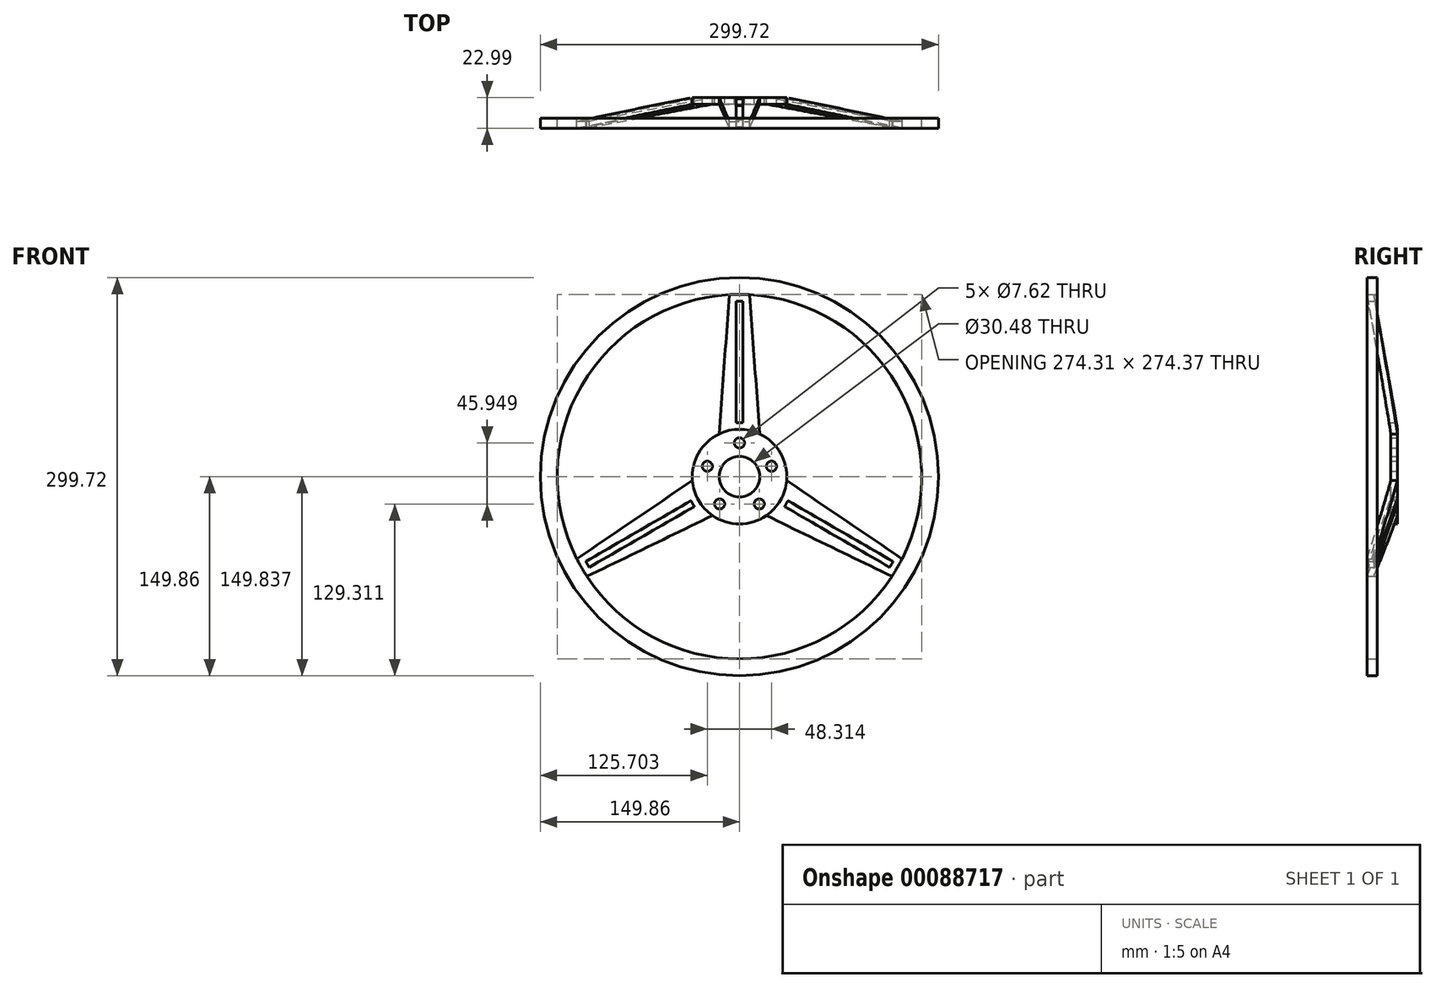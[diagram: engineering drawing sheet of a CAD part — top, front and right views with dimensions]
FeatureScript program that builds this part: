
annotation { "Feature Type Name" : "Feature", "Feature Type Description" : "" }
export const myFeature = defineFeature(function(context is Context, id is Id, definition is map)
    precondition{}
    {
        {
            var Q0;
            Q0=qCreatedBy(makeId("Top.planeOp"),FACE);
            var sketch = newSketch(context, id + "F0", { "sketchPlane" : qUnion([Q0])});
            skLineSegment(sketch, "E0", {"start": v(0, 33.06) * mm, "end": v(0, -40.5) * mm});
            skLineSegment(sketch, "E1.bottom", {"start": v(-15.24, 0) * mm, "end": v(-35.56, 0) * mm});
            skLineSegment(sketch, "E1.top", {"start": v(-15.24, -5.08) * mm, "end": v(-35.6, -5.08) * mm});
            skLineSegment(sketch, "E1.left", {"start": v(-15.24, 0) * mm, "end": v(-15.24, -5.08) * mm});
            skLineSegment(sketch, "E2", {"start": v(-35.56, 0) * mm, "end": v(-137.16, -17.91) * mm});
            skLineSegment(sketch, "E3", {"start": v(-35.6, -5.08) * mm, "end": v(-137.16, -22.99) * mm});
            skLineSegment(sketch, "E4.bottom", {"start": v(-137.16, -22.99) * mm, "end": v(-149.86, -22.99) * mm});
            skLineSegment(sketch, "E4.top", {"start": v(-137.16, -15.37) * mm, "end": v(-149.86, -15.37) * mm});
            skLineSegment(sketch, "E4.left", {"start": v(-137.16, -17.91) * mm, "end": v(-137.16, -15.37) * mm});
            skLineSegment(sketch, "E4.right", {"start": v(-149.86, -22.99) * mm, "end": v(-149.86, -15.37) * mm});
            skSolve(sketch);
        }
        {
            var Q0;
            Q0=makeQuery(id+"F0.imprint","IMPRINT",FACE,{"disambiguationData":[TD([[makeQuery(id+"F0.imprint","IMPRINT",EDGE,{"derivedFrom":sQuery(id+"F0.wireOp",EDGE,"E1.bottom")}),1.0]])]});
            var Q1;
            Q1=sQuery(id+"F0.wireOp",EDGE,"E0");
            revolve(context, id + "F1", {"entities" : qUnion([Q0]), "axis" : qUnion([Q1]), "revolveType" : RevolveType.FULL});
        }
        {
            var Q0;
            Q0=makeQuery(id+"F1.opRevolve","SWEPT_FACE",FACE,{"disambiguationData":[OSD([sQuery(id+"F0.wireOp",EDGE,"E1.top")])]});
            var sketch = newSketch(context, id + "F2", { "sketchPlane" : qUnion([Q0])});
            skLineSegment(sketch, "E5", {"start": v(0, 35.6) * mm, "end": v(0, 137.2) * mm});
            skLineSegment(sketch, "E6", {"start": v(0, 137.2) * mm, "end": v(-7.62, 137.2) * mm});
            skLineSegment(sketch, "E7", {"start": v(0, 137.2) * mm, "end": v(7.62, 137.2) * mm});
            skLineSegment(sketch, "E8", {"start": v(-7.62, 137.2) * mm, "end": v(-15.24, 32.18) * mm});
            skLineSegment(sketch, "E9", {"start": v(7.62, 137.2) * mm, "end": v(15.24, 32.18) * mm});
            skLineSegment(sketch, "E10.1.0", {"start": v(-115.01, -75.2) * mm, "end": v(-20.25, -29.29) * mm});
            skLineSegment(sketch, "E10.1.1", {"start": v(-30.84, -17.8) * mm, "end": v(-118.82, -68.6) * mm});
            skLineSegment(sketch, "E10.1.2", {"start": v(-122.63, -62) * mm, "end": v(-35.49, -2.9) * mm});
            skLineSegment(sketch, "E10.1.3", {"start": v(-118.82, -68.6) * mm, "end": v(-122.63, -62) * mm});
            skLineSegment(sketch, "E10.1.4", {"start": v(-118.82, -68.6) * mm, "end": v(-115.01, -75.2) * mm});
            skLineSegment(sketch, "E10.2.0", {"start": v(122.63, -62) * mm, "end": v(35.49, -2.9) * mm});
            skLineSegment(sketch, "E10.2.1", {"start": v(30.84, -17.8) * mm, "end": v(118.82, -68.6) * mm});
            skLineSegment(sketch, "E10.2.2", {"start": v(115.01, -75.2) * mm, "end": v(20.25, -29.29) * mm});
            skLineSegment(sketch, "E10.2.3", {"start": v(118.82, -68.6) * mm, "end": v(115.01, -75.2) * mm});
            skLineSegment(sketch, "E10.2.4", {"start": v(118.82, -68.6) * mm, "end": v(122.63, -62) * mm});
            skPoint(sketch, "E10.center", {"position": v(0, 0) * mm});
            skLineSegment(sketch, "E11.bottom", {"start": v(2.54, 40.69) * mm, "end": v(-2.54, 40.69) * mm});
            skLineSegment(sketch, "E11.top", {"start": v(2.54, 132.13) * mm, "end": v(-2.54, 132.13) * mm});
            skLineSegment(sketch, "E11.left", {"start": v(2.54, 40.69) * mm, "end": v(2.54, 132.13) * mm});
            skLineSegment(sketch, "E11.right", {"start": v(-2.54, 40.69) * mm, "end": v(-2.54, 132.13) * mm});
            skPoint(sketch, "E11.middle", {"position": v(0, 86.4) * mm});
            skLineSegment(sketch, "E12.1.0", {"start": v(-33.97, -22.54) * mm, "end": v(-113.15, -68.26) * mm});
            skLineSegment(sketch, "E12.1.1", {"start": v(-115.7, -63.86) * mm, "end": v(-113.15, -68.26) * mm});
            skLineSegment(sketch, "E12.1.2", {"start": v(-36.5, -18.14) * mm, "end": v(-115.7, -63.86) * mm});
            skLineSegment(sketch, "E12.1.3", {"start": v(-36.5, -18.14) * mm, "end": v(-33.97, -22.54) * mm});
            skLineSegment(sketch, "E12.2.0", {"start": v(36.5, -18.14) * mm, "end": v(115.7, -63.86) * mm});
            skLineSegment(sketch, "E12.2.1", {"start": v(113.15, -68.26) * mm, "end": v(115.7, -63.86) * mm});
            skLineSegment(sketch, "E12.2.2", {"start": v(33.97, -22.54) * mm, "end": v(113.15, -68.26) * mm});
            skLineSegment(sketch, "E12.2.3", {"start": v(33.97, -22.54) * mm, "end": v(36.5, -18.14) * mm});
            skCircle(sketch, "E13", {"center": v(0, 0) * mm, "radius": 137.2 * mm});
            skCircle(sketch, "E14", {"center": v(0, 25.4) * mm, "radius": 3.81 * mm});
            skCircle(sketch, "E15.1.0", {"center": v(-24.16, 7.85) * mm, "radius": 3.8 * mm});
            skCircle(sketch, "E15.2.0", {"center": v(-14.93, -20.55) * mm, "radius": 3.81 * mm});
            skCircle(sketch, "E16.1.3.0", {"center": v(14.93, -20.55) * mm, "radius": 3.81 * mm});
            skCircle(sketch, "E16.1.4.0", {"center": v(24.16, 7.85) * mm, "radius": 3.81 * mm});
            skSolve(sketch);
        }
        {
            var Q0;
            {var subQ5=sQuery(id+"F2.wireOp",EDGE,"E12.1.2");Q0=makeQuery(id+"F2.imprint","IMPRINT",FACE,{"disambiguationData":[TD([[makeQuery(id+"F2.imprint","IMPRINT",EDGE,{"derivedFrom":subQ5}),1.0]])]});}
            var Q1;
            {var subQ5=sQuery(id+"F2.wireOp",EDGE,"E12.1.0");Q1=makeQuery(id+"F2.imprint","IMPRINT",FACE,{"disambiguationData":[TD([[makeQuery(id+"F2.imprint","IMPRINT",EDGE,{"derivedFrom":subQ5}),-1.0]])]});}
            var Q2;
            {var subQ5=sQuery(id+"F2.wireOp",EDGE,"E11.right");Q2=makeQuery(id+"F2.imprint","IMPRINT",FACE,{"disambiguationData":[TD([[makeQuery(id+"F2.imprint","IMPRINT",EDGE,{"derivedFrom":subQ5}),-1.0]])]});}
            var Q3;
            {var subQ5=sQuery(id+"F2.wireOp",EDGE,"E11.left");Q3=makeQuery(id+"F2.imprint","IMPRINT",FACE,{"disambiguationData":[TD([[makeQuery(id+"F2.imprint","IMPRINT",EDGE,{"derivedFrom":subQ5}),1.0]])]});}
            var Q4;
            {var subQ5=sQuery(id+"F2.wireOp",EDGE,"E12.2.2");Q4=makeQuery(id+"F2.imprint","IMPRINT",FACE,{"disambiguationData":[TD([[makeQuery(id+"F2.imprint","IMPRINT",EDGE,{"derivedFrom":subQ5}),1.0]])]});}
            var Q5;
            {var subQ5=sQuery(id+"F2.wireOp",EDGE,"E12.2.0");Q5=makeQuery(id+"F2.imprint","IMPRINT",FACE,{"disambiguationData":[TD([[makeQuery(id+"F2.imprint","IMPRINT",EDGE,{"derivedFrom":subQ5}),-1.0]])]});}
            var Q6;
            Q6=makeQuery(id+"F2.imprint","IMPRINT",FACE,{"disambiguationData":[TD([[makeQuery(id+"F2.imprint","IMPRINT",EDGE,{"derivedFrom":sQuery(id+"F2.wireOp",EDGE,"E14")}),1.0]])]});
            var Q7;
            Q7=makeQuery(id+"F2.imprint","IMPRINT",FACE,{"disambiguationData":[TD([[makeQuery(id+"F2.imprint","IMPRINT",EDGE,{"derivedFrom":sQuery(id+"F2.wireOp",EDGE,"E15.1.0")}),1.0]])]});
            var Q8;
            Q8=makeQuery(id+"F2.imprint","IMPRINT",FACE,{"disambiguationData":[TD([[makeQuery(id+"F2.imprint","IMPRINT",EDGE,{"derivedFrom":sQuery(id+"F2.wireOp",EDGE,"E16.1.4.0")}),1.0]])]});
            var Q9;
            Q9=makeQuery(id+"F2.imprint","IMPRINT",FACE,{"disambiguationData":[TD([[makeQuery(id+"F2.imprint","IMPRINT",EDGE,{"derivedFrom":sQuery(id+"F2.wireOp",EDGE,"E16.1.3.0")}),1.0]])]});
            var Q10;
            Q10=makeQuery(id+"F2.imprint","IMPRINT",FACE,{"disambiguationData":[TD([[makeQuery(id+"F2.imprint","IMPRINT",EDGE,{"derivedFrom":sQuery(id+"F2.wireOp",EDGE,"E15.2.0")}),1.0]])]});
            extrude(context, id + "F3", {"entities" : qUnion([Q0, Q1, Q2, Q3, Q4, Q5, Q6, Q7, Q8, Q9, Q10]), "operationType" : NewBodyOperationType.REMOVE, "endBound" : BoundingType.THROUGH_ALL, "depth" : 25.4 * mm, "hasSecondDirection" : true, "secondDirectionBound" : SecondDirectionBoundingType.THROUGH_ALL, "secondDirectionOppositeDirection" : true, "secondDirectionDepth" : 25.4 * mm});
        }
        {
            var Q0;
            {var subQ0=sQuery(id+"F2.wireOp",EDGE,"E9");var subQ3=sQuery(id+"F2.wireOp",EDGE,"E13");var subQ4=makeQuery(id+"F2.imprint","INTERSECT",VERTEX,{"derivedFrom":[subQ0,subQ3]});Q0=makeQuery(id+"F2.imprint","IMPRINT",FACE,{"disambiguationData":[TD([[makeQuery(id+"F2.imprint","IMPRINT",EDGE,{"disambiguationData":[TD([[subQ4,1.0]])],"derivedFrom":subQ3}),1.0]])]});}
            var Q1;
            {var subQ0=sQuery(id+"F2.wireOp",EDGE,"E8");var subQ3=sQuery(id+"F2.wireOp",EDGE,"E13");var subQ4=makeQuery(id+"F2.imprint","INTERSECT",VERTEX,{"derivedFrom":[subQ0,subQ3]});Q1=makeQuery(id+"F2.imprint","IMPRINT",FACE,{"disambiguationData":[TD([[makeQuery(id+"F2.imprint","IMPRINT",EDGE,{"disambiguationData":[TD([[subQ4,-1.0]])],"derivedFrom":subQ3}),1.0]])]});}
            var Q2;
            {var subQ0=sQuery(id+"F2.wireOp",EDGE,"E10.1.0");var subQ3=sQuery(id+"F2.wireOp",EDGE,"E13");var subQ4=makeQuery(id+"F2.imprint","INTERSECT",VERTEX,{"derivedFrom":[subQ0,subQ3]});Q2=makeQuery(id+"F2.imprint","IMPRINT",FACE,{"disambiguationData":[TD([[makeQuery(id+"F2.imprint","IMPRINT",EDGE,{"disambiguationData":[TD([[subQ4,-1.0]])],"derivedFrom":subQ3}),1.0]])]});}
            extrude(context, id + "F4", {"entities" : qUnion([Q0, Q1, Q2]), "operationType" : NewBodyOperationType.REMOVE, "endBound" : BoundingType.THROUGH_ALL, "depth" : 25.4 * mm, "hasSecondDirection" : true, "secondDirectionBound" : SecondDirectionBoundingType.THROUGH_ALL, "secondDirectionOppositeDirection" : true, "secondDirectionDepth" : 25.4 * mm});
        }
    });
